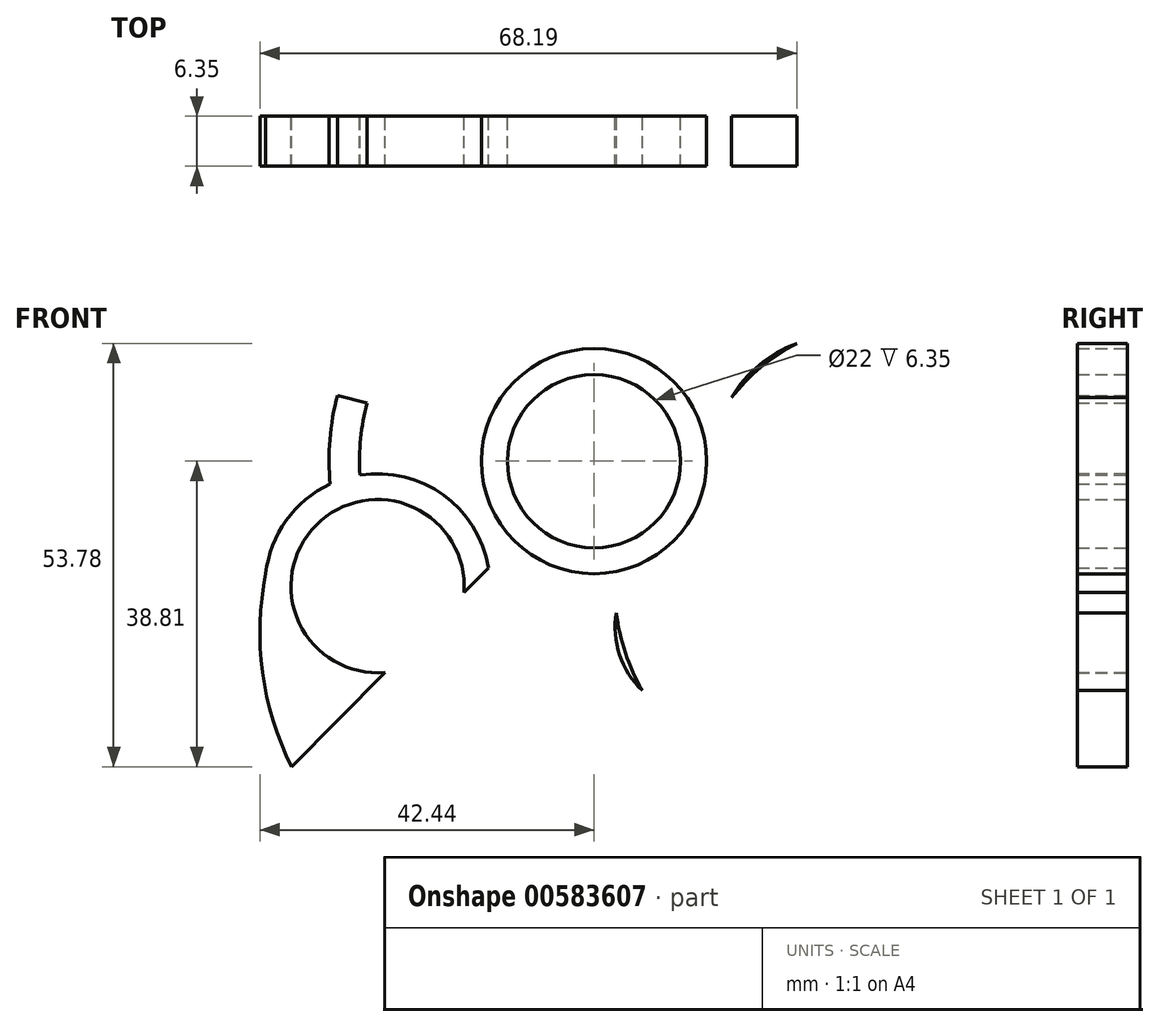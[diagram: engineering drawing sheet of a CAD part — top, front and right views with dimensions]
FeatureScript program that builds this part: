
annotation { "Feature Type Name" : "Feature", "Feature Type Description" : "" }
export const myFeature = defineFeature(function(context is Context, id is Id, definition is map)
    precondition{}
    {
        {
            var Q0;
            Q0=qCreatedBy(makeId("Front.planeOp"),FACE);
            var sketch = newSketch(context, id + "F0", { "sketchPlane" : qUnion([Q0])});
            skCircle(sketch, "E0", {"center": v(0, 31.75) * mm, "radius": 11 * mm});
            skCircle(sketch, "E1", {"center": v(0, 31.75) * mm, "radius": 14.29 * mm});
            skCircle(sketch, "E2", {"center": v(0, 0) * mm, "radius": 14.3 * mm});
            skCircle(sketch, "E3", {"center": v(0, 0) * mm, "radius": 11 * mm});
            skCircle(sketch, "E4.1.2", {"center": v(-27.5, -15.87) * mm, "radius": 14.29 * mm});
            skCircle(sketch, "E4.1.3", {"center": v(-27.5, -15.87) * mm, "radius": 11 * mm});
            skCircle(sketch, "E4.2.2", {"center": v(27.5, -15.88) * mm, "radius": 14.29 * mm});
            skCircle(sketch, "E4.2.3", {"center": v(27.5, -15.88) * mm, "radius": 11 * mm});
            skSolve(sketch);
        }
        {
            var Q0;
            Q0=qCreatedBy(makeId("Front.planeOp"),FACE);
            var sketch = newSketch(context, id + "F1", { "sketchPlane" : qUnion([Q0])});
            skCircle(sketch, "E5.0", {"center": v(0, 0) * mm, "radius": 11 * mm});
            skArc(sketch, "E5.1", {"start": v(-33.53, -2.92) * mm, "mid": v(-39.1, -7.54) * mm, "end": v(-41.7, -14.29) * mm});
            skArc(sketch, "E5.2", {"start": v(19.3, -27.58) * mm, "mid": v(26.08, -30.1) * mm, "end": v(33.22, -28.97) * mm});
            skArc(sketch, "E5.3", {"start": v(11, 31.8) * mm, "mid": v(0, 42.75) * mm, "end": v(-11, 31.8) * mm});
            skArc(sketch, "E5.4", {"start": v(14.23, 30.5) * mm, "mid": v(13.02, 37.63) * mm, "end": v(8.48, 43.25) * mm});
            skArc(sketch, "E5.5", {"start": v(22.05, -25.43) * mm, "mid": v(37.02, -21.37) * mm, "end": v(33.05, -6.38) * mm});
            skCircle(sketch, "E5.6", {"center": v(0, 0) * mm, "radius": 14.3 * mm});
            skArc(sketch, "E5.7", {"start": v(-33.05, -6.38) * mm, "mid": v(-37.02, -21.37) * mm, "end": v(-22.05, -25.43) * mm});
            skCircle(sketch, "E5.8", {"center": v(0, 0) * mm, "radius": 11 * mm});
            skCircle(sketch, "E5.9", {"center": v(0, 0) * mm, "radius": 14.3 * mm});
            skCircle(sketch, "E5.10", {"center": v(0, 0) * mm, "radius": 14.3 * mm});
            skCircle(sketch, "E5.11", {"center": v(0, 0) * mm, "radius": 11 * mm});
            skArc(sketch, "E6", {"start": v(-29.74, -1.58) * mm, "mid": v(-23.27, 1.94) * mm, "end": v(-18.1, 7.17) * mm});
            skArc(sketch, "E7", {"start": v(13.5, 26.55) * mm, "mid": v(13.32, 19.19) * mm, "end": v(15.26, 12.08) * mm});
            skArc(sketch, "E8", {"start": v(16.24, -24.97) * mm, "mid": v(9.96, -21.13) * mm, "end": v(2.83, -19.25) * mm});
            skArc(sketch, "E9", {"start": v(-13.34, 26.63) * mm, "mid": v(-20.46, 21.64) * mm, "end": v(-25.84, 14.81) * mm});
            skArc(sketch, "E10", {"start": v(-14.23, 30.5) * mm, "mid": v(-29.15, 16.83) * mm, "end": v(-33.53, -2.92) * mm});
            skArc(sketch, "E11.trimOffspring", {"start": v(-10.32, 27.94) * mm, "mid": v(0, 20.75) * mm, "end": v(10.32, 27.94) * mm});
            skArc(sketch, "E12.trimOffspring", {"start": v(-13.34, 26.63) * mm, "mid": v(0, 17.46) * mm, "end": v(13.34, 26.63) * mm});
            skArc(sketch, "E13.trimOffspring", {"start": v(-19.04, -22.9) * mm, "mid": v(-17.97, -10.38) * mm, "end": v(-29.36, -5.04) * mm});
            skArc(sketch, "E14.trimOffspring", {"start": v(-16.4, -24.87) * mm, "mid": v(-8.51, -28.54) * mm, "end": v(0.1, -29.78) * mm});
            skArc(sketch, "E15.trimOffspring", {"start": v(-19.3, -27.58) * mm, "mid": v(0, -33.66) * mm, "end": v(19.3, -27.58) * mm});
            skArc(sketch, "E16.trimOffspring", {"start": v(-16.4, -24.87) * mm, "mid": v(-15.12, -8.73) * mm, "end": v(-29.73, -1.76) * mm});
            skArc(sketch, "E17.trimOffspring", {"start": v(29.36, -5.04) * mm, "mid": v(17.97, -10.38) * mm, "end": v(19.04, -22.9) * mm});
            skArc(sketch, "E18.trimOffspring", {"start": v(33.53, -2.92) * mm, "mid": v(29.15, 16.83) * mm, "end": v(14.23, 30.5) * mm});
            skArc(sketch, "E19.trimOffspring", {"start": v(29.74, -1.58) * mm, "mid": v(28.95, 6.98) * mm, "end": v(25.75, 14.97) * mm});
            skArc(sketch, "E20.trimOffspring", {"start": v(29.73, -1.76) * mm, "mid": v(15.12, -8.73) * mm, "end": v(16.4, -24.87) * mm});
            skText(sketch, "E21", { "text": "SN", "fontName": "Tinos-BoldItalic.ttf"});
            skCircle(sketch, "E22.0", {"center": v(-27.5, -15.87) * mm, "radius": 11 * mm});
            skCircle(sketch, "E23.0", {"center": v(27.5, -15.88) * mm, "radius": 11 * mm});
            skCircle(sketch, "E24.0", {"center": v(0, 31.75) * mm, "radius": 11 * mm});
            skArc(sketch, "E25", {"start": v(8.48, 43.25) * mm, "mid": v(-8.49, 51.85) * mm, "end": v(-27.5, 51.13) * mm});
            skArc(sketch, "E26", {"start": v(-14.23, 30.5) * mm, "mid": v(-18.2, 42.52) * mm, "end": v(-27.5, 51.13) * mm});
            skLineSegment(sketch, "E27.trimOffspring", {"start": v(-14.23, 30.5) * mm, "end": v(-14.23, 30.5) * mm});
            skArc(sketch, "E28.1.0", {"start": v(-19.3, -27.58) * mm, "mid": v(-27.72, -37.03) * mm, "end": v(-30.53, -49.37) * mm});
            skArc(sketch, "E28.1.1", {"start": v(-41.7, -14.29) * mm, "mid": v(-40.66, -33.28) * mm, "end": v(-30.53, -49.37) * mm});
            skArc(sketch, "E28.2.0", {"start": v(33.53, -2.92) * mm, "mid": v(45.93, -5.5) * mm, "end": v(58.02, -1.75) * mm});
            skArc(sketch, "E28.2.1", {"start": v(33.22, -28.97) * mm, "mid": v(49.15, -18.58) * mm, "end": v(58.02, -1.75) * mm});
            skArc(sketch, "E29.trimOffspring", {"start": v(-19.6, -27.78) * mm, "mid": v(-19.45, -27.68) * mm, "end": v(-19.3, -27.58) * mm});
            skArc(sketch, "E30.trimOffspring", {"start": v(33.86, -3.08) * mm, "mid": v(33.7, -3) * mm, "end": v(33.53, -2.92) * mm});
            skArc(sketch, "E31", {"start": v(25.75, 14.97) * mm, "mid": v(21.24, 11.96) * mm, "end": v(17.46, 8.07) * mm});
            skArc(sketch, "E32", {"start": v(15.26, 12.08) * mm, "mid": v(19.11, 15.63) * mm, "end": v(22.18, 19.88) * mm});
            skArc(sketch, "E33.2.0", {"start": v(2.83, -19.25) * mm, "mid": v(3.98, -24.37) * mm, "end": v(6.13, -29.15) * mm});
            skArc(sketch, "E33.2.1", {"start": v(0.1, -29.78) * mm, "mid": v(-0.26, -24.37) * mm, "end": v(-1.74, -19.15) * mm});
            skArc(sketch, "E34.trimOffspring", {"start": v(-28.3, 9.27) * mm, "mid": v(-29.54, 3.82) * mm, "end": v(-29.73, -1.76) * mm});
            skArc(sketch, "E35.trimOffspring", {"start": v(-15.72, 11.08) * mm, "mid": v(-13.4, 18.64) * mm, "end": v(-13.5, 26.55) * mm});
            skArc(sketch, "E36.trimOffspring", {"start": v(17.46, 8.07) * mm, "mid": v(22.84, 2.28) * mm, "end": v(29.74, -1.58) * mm});
            skArc(sketch, "E37.trimOffspring", {"start": v(22.18, 19.88) * mm, "mid": v(18.08, 23.67) * mm, "end": v(13.34, 26.63) * mm});
            skArc(sketch, "E38.trimOffspring", {"start": v(-1.74, -19.15) * mm, "mid": v(-9.45, -20.92) * mm, "end": v(-16.24, -24.97) * mm});
            skArc(sketch, "E39.trimOffspring", {"start": v(6.13, -29.15) * mm, "mid": v(11.46, -27.5) * mm, "end": v(16.4, -24.87) * mm});
            skArc(sketch, "E40", {"start": v(-18.1, 7.17) * mm, "mid": v(-22.94, 9.48) * mm, "end": v(-28.3, 9.27) * mm});
            skArc(sketch, "E41", {"start": v(-25.84, 14.81) * mm, "mid": v(-21.1, 12.08) * mm, "end": v(-15.72, 11.08) * mm});
            skLineSegment(sketch, "E42", {"start": v(-77, 75.96) * mm, "end": v(74.91, -74.39) * mm});
            skLineSegment(sketch, "E43", {"start": v(74.91, -74.39) * mm, "end": v(74.91, 76.48) * mm});
            skLineSegment(sketch, "E44", {"start": v(74.91, 76.48) * mm, "end": v(0, 0) * mm});
            skLineSegment(sketch, "E45", {"start": v(0, 0) * mm, "end": v(-75.17, -75.96) * mm});
            skLineSegment(sketch, "E46", {"start": v(-77, 75.7) * mm, "end": v(-77, -79.62) * mm});
            skLineSegment(sketch, "E47", {"start": v(-77, -79.62) * mm, "end": v(-75.17, -75.96) * mm});
            skLineSegment(sketch, "E48", {"start": v(74.91, -74.39) * mm, "end": v(-75.17, -75.96) * mm});
            skArc(sketch, "E49.1.2", {"start": v(-13.5, 26.55) * mm, "mid": v(-20.53, 21.58) * mm, "end": v(-25.84, 14.81) * mm});
            skArc(sketch, "E49.1.16", {"start": v(0.1, -29.78) * mm, "mid": v(0.1, -24.31) * mm, "end": v(-1.74, -19.15) * mm});
            skArc(sketch, "E49.1.20", {"start": v(29.73, -1.76) * mm, "mid": v(28.97, 6.9) * mm, "end": v(25.75, 14.97) * mm});
            skArc(sketch, "E49.1.24", {"start": v(2.83, -19.25) * mm, "mid": v(3.26, -24.6) * mm, "end": v(6.13, -29.15) * mm});
            skArc(sketch, "E49.1.29", {"start": v(-25.84, 14.81) * mm, "mid": v(-20.97, 12.42) * mm, "end": v(-15.72, 11.08) * mm});
            skLineSegment(sketch, "E49.1.31", {"start": v(-103.69, 26.64) * mm, "end": v(0, 0) * mm});
            skArc(sketch, "E49.1.39", {"start": v(-18.1, 7.17) * mm, "mid": v(-23.1, 8.74) * mm, "end": v(-28.3, 9.27) * mm});
            skArc(sketch, "E49.1.46", {"start": v(-14.26, 30.87) * mm, "mid": v(-14.25, 30.68) * mm, "end": v(-14.23, 30.5) * mm});
            skArc(sketch, "E49.2.2", {"start": v(-16.24, -24.97) * mm, "mid": v(-8.43, -28.57) * mm, "end": v(0.1, -29.78) * mm});
            skArc(sketch, "E49.2.16", {"start": v(25.75, 14.97) * mm, "mid": v(21, 12.23) * mm, "end": v(17.46, 8.07) * mm});
            skArc(sketch, "E49.2.22", {"start": v(-18.1, 7.17) * mm, "mid": v(-23.1, 8.74) * mm, "end": v(-28.3, 9.27) * mm});
            skArc(sketch, "E49.2.24", {"start": v(15.26, 12.08) * mm, "mid": v(19.68, 15.13) * mm, "end": v(22.18, 19.88) * mm});
            skLineSegment(sketch, "E49.2.31", {"start": v(28.78, -103.12) * mm, "end": v(0, 0) * mm});
            skArc(sketch, "E49.2.32", {"start": v(29.73, -1.76) * mm, "mid": v(28.97, 6.9) * mm, "end": v(25.75, 14.97) * mm});
            skArc(sketch, "E49.2.38", {"start": v(-25.84, 14.81) * mm, "mid": v(-20.97, 12.42) * mm, "end": v(-15.72, 11.08) * mm});
            skArc(sketch, "E49.2.47", {"start": v(-14.26, 30.87) * mm, "mid": v(-14.25, 30.68) * mm, "end": v(-14.23, 30.5) * mm});
            const initialGuessF1  = {"E21": [-0.00272, -0.01745, 1, 0, 0.00303]};
            skSetInitialGuess(sketch, initialGuessF1);
            skSolve(sketch);
        }
        {
            var Q0;
            Q0=makeQuery(id+"F1.imprint","IMPRINT",FACE,{"disambiguationData":[TD([[makeQuery(id+"F1.imprint","IMPRINT",EDGE,{"derivedFrom":sQuery(id+"F1.wireOp",EDGE,"E5.1")}),1.0]])]});
            var Q1;
            {var subQ0=sQuery(id+"F1.wireOp",EDGE,"E31");Q1=makeQuery(id+"F1.imprint","IMPRINT",FACE,{"disambiguationData":[TD([[makeQuery(id+"F1.imprint","IMPRINT",EDGE,{"derivedFrom":subQ0}),-1.0]])]});}
            var Q2;
            {var subQ0=sQuery(id+"F1.wireOp",EDGE,"E33.2.0");Q2=makeQuery(id+"F1.imprint","IMPRINT",FACE,{"disambiguationData":[TD([[makeQuery(id+"F1.imprint","IMPRINT",EDGE,{"derivedFrom":subQ0}),-1.0]])]});}
            var Q3;
            {var subQ0=sQuery(id+"F1.wireOp",EDGE,"E33.1.0");Q3=makeQuery(id+"F1.imprint","IMPRINT",FACE,{"disambiguationData":[TD([[makeQuery(id+"F1.imprint","IMPRINT",EDGE,{"derivedFrom":subQ0}),-1.0]])]});}
            extrude(context, id + "F2", {"entities" : qUnion([Q0, Q1, Q2, Q3]), "depth" : 6.35 * mm, "offsetDistance" : 25.4 * mm});
        }
        {
            var Q0;
            Q0=makeQuery(id+"F0.imprint","IMPRINT",FACE,{"disambiguationData":[TD([[makeQuery(id+"F0.imprint","IMPRINT",EDGE,{"derivedFrom":sQuery(id+"F0.wireOp",EDGE,"E3")}),-1.0]])]});
            extrude(context, id + "F3", {"entities" : qUnion([Q0]), "depth" : 6.35 * mm, "offsetDistance" : 25.4 * mm});
        }
    });
